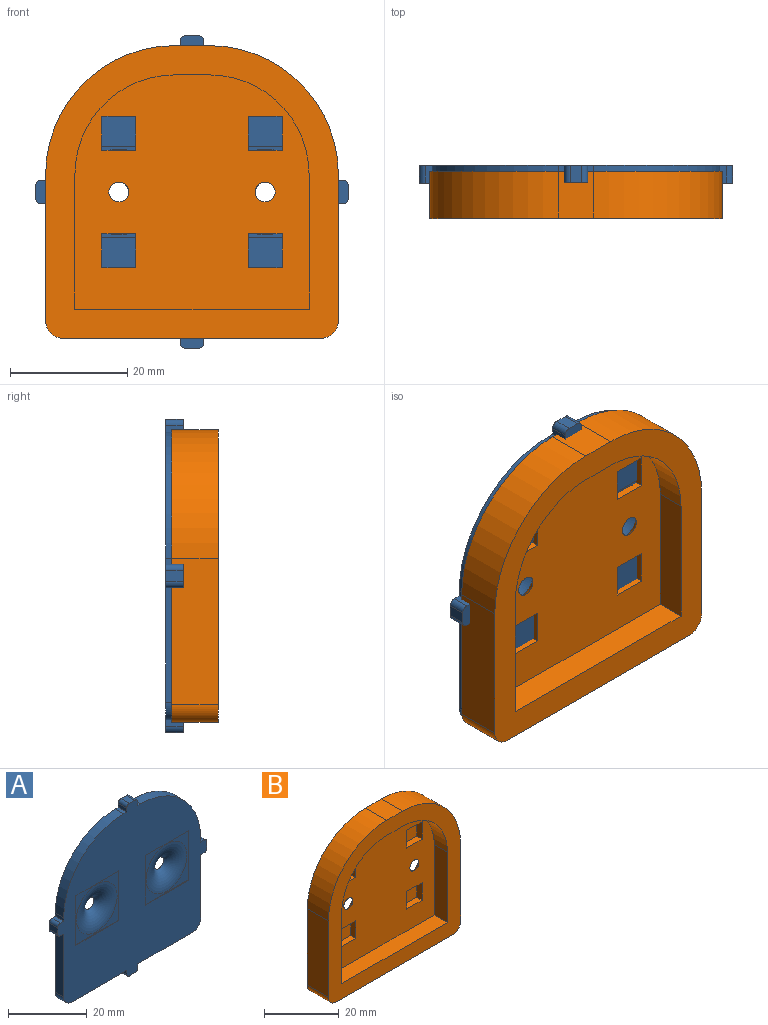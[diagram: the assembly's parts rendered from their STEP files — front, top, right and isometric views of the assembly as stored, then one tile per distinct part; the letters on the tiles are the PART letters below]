
ASSEMBLY  parts=2 mates=1
PART A: 66 faces, bbox 53.5x7.2x53.5 mm
  f0: plane 53.5x53.5mm, normal (0,-1,0), area 1767.7mm2, adj f2,f3,f4,f5,f6,f7,f8,f9
  f1: plane 53.5x53.5mm, normal (0,1,0), area 2089.3mm2, adj f2,f3,f4,f5,f6,f7,f8,f9
  f2: plane 19.55x3mm, normal (0,0,-1), area 58.6mm2, adj f0,f1,f3,f24
  f3: plane 3x1.2mm, normal (-1,0,0), area 3.6mm2, adj f0,f1,f2,f58
  f4: plane 3x2mm, normal (0,0,-1), area 6mm2, adj f0,f1,f58,f59
  f5: plane 3x1.2mm, normal (1,0,0), area 3.6mm2, adj f0,f1,f6,f59
  f6: plane 19.55x3mm, normal (0,0,-1), area 58.6mm2, adj f0,f1,f5,f25
  f7: plane 19.55x3mm, normal (1,0,0), area 58.6mm2, adj f0,f1,f8,f25
  f8: plane 3x1.2mm, normal (0,0,-1), area 3.6mm2, adj f0,f1,f7,f62
  f9: plane 3x2mm, normal (1,0,0), area 6mm2, adj f0,f1,f62,f63
  f10: plane 3x1.2mm, normal (0,0,1), area 3.6mm2, adj f0,f1,f11,f63
  f11: plane 3x1.05mm, normal (1,0,0), area 3.1mm2, adj f0,f1,f10,f12
  f12: cylinder r=21.5mm len=21.5mm, axis (0,1,0), area 101.3mm2, adj f0,f1,f11,f13
  f13: plane 3x1.05mm, normal (0,0,1), area 3.1mm2, adj f0,f1,f12,f14
  f14: plane 3x1.2mm, normal (1,0,0), area 3.6mm2, adj f0,f1,f13,f60
  f15: plane 3x2mm, normal (0,0,1), area 6mm2, adj f0,f1,f60,f61
  f16: plane 3x1.2mm, normal (-1,0,0), area 3.6mm2, adj f0,f1,f17,f61
  f17: plane 3x1.05mm, normal (0,0,1), area 3.2mm2, adj f0,f1,f16,f18
  f18: cylinder r=21.5mm len=21.5mm, axis (0,1,0), area 101.3mm2, adj f0,f1,f17,f19
  f19: plane 3x1.05mm, normal (-1,0,0), area 3.1mm2, adj f0,f1,f18,f20
  f20: plane 3x1.2mm, normal (0,0,1), area 3.6mm2, adj f0,f1,f19,f64
  f21: plane 3x2mm, normal (-1,0,0), area 6mm2, adj f0,f1,f64,f65
  f22: plane 3x1.2mm, normal (0,0,-1), area 3.6mm2, adj f0,f1,f23,f65
  f23: plane 19.55x3mm, normal (-1,0,0), area 58.6mm2, adj f0,f1,f22,f24
  f24: cylinder r=3mm len=3mm, axis (0,1,0), area 14.1mm2, adj f0,f1,f2,f23
  f25: cylinder r=3mm len=3mm, axis (0,-1,0), area 14.1mm2, adj f0,f1,f6,f7
  f26: plane 5.8x2mm, normal (0,0,1), area 11.6mm2, adj f1,f27,f29,f30
  f27: plane 5.8x2mm, normal (1,0,0), area 11.6mm2, adj f1,f26,f28,f30
  f28: plane 5.8x2mm, normal (0,0,-1), area 11.6mm2, adj f1,f27,f29,f30
  f29: plane 5.8x2mm, normal (-1,0,0), area 11.6mm2, adj f1,f26,f28,f30
  f30: plane 5.8x5.8mm, normal (0,1,0), area 33.6mm2, adj f26,f27,f28,f29
  f31: plane 5.8x2mm, normal (1,0,0), area 11.6mm2, adj f1,f32,f34,f35
  f32: plane 5.8x2mm, normal (0,0,-1), area 11.6mm2, adj f1,f31,f33,f35
  f33: plane 5.8x2mm, normal (-1,0,0), area 11.6mm2, adj f1,f32,f34,f35
  f34: plane 5.8x2mm, normal (0,0,1), area 11.6mm2, adj f1,f31,f33,f35
  f35: plane 5.8x5.8mm, normal (0,1,0), area 33.6mm2, adj f31,f32,f33,f34
  f36: plane 5.8x2mm, normal (0,0,1), area 11.6mm2, adj f1,f37,f39,f40
  f37: plane 5.8x2mm, normal (1,0,0), area 11.6mm2, adj f1,f36,f38,f40
  f38: plane 5.8x2mm, normal (0,0,-1), area 11.6mm2, adj f1,f37,f39,f40
  f39: plane 5.8x2mm, normal (-1,0,0), area 11.6mm2, adj f1,f36,f38,f40
  f40: plane 5.8x5.8mm, normal (0,1,0), area 33.6mm2, adj f36,f37,f38,f39
  f41: plane 5.8x2mm, normal (0,0,1), area 11.6mm2, adj f1,f42,f44,f45
  f42: plane 5.8x2mm, normal (1,0,0), area 11.6mm2, adj f1,f41,f43,f45
  f43: plane 5.8x2mm, normal (0,0,-1), area 11.6mm2, adj f1,f42,f44,f45
  f44: plane 5.8x2mm, normal (-1,0,0), area 11.6mm2, adj f1,f41,f43,f45
  f45: plane 5.8x5.8mm, normal (0,1,0), area 33.6mm2, adj f41,f42,f43,f44
  f46: plane 15.4x0.2mm, normal (0,0,-1), area 3.1mm2, adj f0,f47,f49,f50
  f47: plane 15.4x0.2mm, normal (1,0,0), area 3.1mm2, adj f0,f46,f48,f50
  f48: plane 15.4x0.2mm, normal (0,0,1), area 3.1mm2, adj f0,f47,f49,f50
  f49: plane 15.4x0.2mm, normal (-1,0,0), area 3.1mm2, adj f0,f46,f48,f50
  f50: plane 15.4x15.4mm, normal (0,-1,0), area 69.7mm2, adj f46,f47,f48,f49,f56
  f51: plane 15.4x0.2mm, normal (0,0,-1), area 3.1mm2, adj f0,f52,f54,f55
  f52: plane 15.4x0.2mm, normal (1,0,0), area 3.1mm2, adj f0,f51,f53,f55
  f53: plane 15.4x0.2mm, normal (0,0,1), area 3.1mm2, adj f0,f52,f54,f55
  f54: plane 15.4x0.2mm, normal (-1,0,0), area 3.1mm2, adj f0,f51,f53,f55
  f55: plane 15.4x15.4mm, normal (0,-1,0), area 69.7mm2, adj f51,f52,f53,f54,f57
  f56: torus R=7.3mm, axis (0,-1,0), area 174.6mm2, adj f1,f50
  f57: torus R=7.3mm, axis (0,-1,0), area 174.6mm2, adj f1,f55
  f58: cylinder r=1mm len=3mm, axis (0,1,0), area 4.7mm2, adj f0,f1,f3,f4
  f59: cylinder r=1mm len=3mm, axis (0,-1,0), area 4.7mm2, adj f0,f1,f4,f5
  f60: cylinder r=1mm len=3mm, axis (0,1,0), area 4.7mm2, adj f0,f1,f14,f15
  f61: cylinder r=1mm len=3mm, axis (0,-1,0), area 4.7mm2, adj f0,f1,f15,f16
  f62: cylinder r=1mm len=3mm, axis (0,-1,0), area 4.7mm2, adj f0,f1,f8,f9
  f63: cylinder r=1mm len=3mm, axis (0,1,0), area 4.7mm2, adj f0,f1,f9,f10
  f64: cylinder r=1mm len=3mm, axis (0,-1,0), area 4.7mm2, adj f0,f1,f20,f21
  f65: cylinder r=1mm len=3mm, axis (0,1,0), area 4.7mm2, adj f0,f1,f21,f22
PART B: 49 faces, bbox 50x8x50 mm
  f0: plane 40x40mm, normal (0,-1,0), area 1323.2mm2, adj f8,f9,f10,f11,f12,f13,f27,f28
  f1: plane 50x50mm, normal (0,1,0), area 1814.1mm2, adj f2,f3,f4,f5,f6,f7,f15,f16
  f2: plane 8x6mm, normal (0,0,1), area 48mm2, adj f1,f3,f7,f14
  f3: cylinder r=22mm len=22mm, axis (0,1,0), area 276.5mm2, adj f1,f2,f4,f14
  f4: plane 25x8mm, normal (-1,0,0), area 200mm2, adj f1,f3,f14,f26
  f5: plane 44x8mm, normal (0,0,-1), area 352mm2, adj f1,f14,f25,f26
  f6: plane 25x8mm, normal (1,0,0), area 200mm2, adj f1,f7,f14,f25
  f7: cylinder r=22mm len=22mm, axis (0,1,0), area 276.5mm2, adj f1,f2,f6,f14
  f8: plane 40x5mm, normal (0,0,1), area 200mm2, adj f0,f9,f13,f14
  f9: plane 23x5mm, normal (1,0,0), area 115mm2, adj f0,f8,f10,f14
  f10: cylinder r=17mm len=17mm, axis (0,1,0), area 133.5mm2, adj f0,f9,f11,f14
  f11: plane 6x5mm, normal (0,0,-1), area 30mm2, adj f0,f10,f12,f14
  f12: cylinder r=17mm len=17mm, axis (0,1,0), area 133.5mm2, adj f0,f11,f13,f14
  f13: plane 23x5mm, normal (-1,0,0), area 115mm2, adj f0,f8,f12,f14
  f14: plane 50x50mm, normal (0,-1,0), area 812.4mm2, adj f2,f3,f4,f5,f6,f7,f8,f9
  f15: plane 15.4x0.2mm, normal (0,0,-1), area 3.1mm2, adj f1,f16,f18,f19
  f16: plane 15.4x0.2mm, normal (-1,0,0), area 3.1mm2, adj f1,f15,f17,f19
  f17: plane 15.4x0.2mm, normal (0,0,1), area 3.1mm2, adj f1,f16,f18,f19
  f18: plane 15.4x0.2mm, normal (1,0,0), area 3.1mm2, adj f1,f15,f17,f19
  f19: plane 15.4x15.4mm, normal (0,1,0), area 69.7mm2, adj f15,f16,f17,f18,f47
  f20: plane 15.4x0.2mm, normal (0,0,-1), area 3.1mm2, adj f1,f21,f23,f24
  f21: plane 15.4x0.2mm, normal (-1,0,0), area 3.1mm2, adj f1,f20,f22,f24
  f22: plane 15.4x0.2mm, normal (0,0,1), area 3.1mm2, adj f1,f21,f23,f24
  f23: plane 15.4x0.2mm, normal (1,0,0), area 3.1mm2, adj f1,f20,f22,f24
  f24: plane 15.4x15.4mm, normal (0,1,0), area 69.7mm2, adj f20,f21,f22,f23,f48
  f25: cylinder r=3mm len=8mm, axis (0,-1,0), area 37.7mm2, adj f1,f5,f6,f14
  f26: cylinder r=3mm len=8mm, axis (0,1,0), area 37.7mm2, adj f1,f4,f5,f14
  f27: plane 5.8x2mm, normal (0,0,1), area 11.6mm2, adj f0,f28,f30,f31
  f28: plane 5.8x2mm, normal (-1,0,0), area 11.6mm2, adj f0,f27,f29,f31
  f29: plane 5.8x2mm, normal (0,0,-1), area 11.6mm2, adj f0,f28,f30,f31
  f30: plane 5.8x2mm, normal (1,0,0), area 11.6mm2, adj f0,f27,f29,f31
  f31: plane 5.8x5.8mm, normal (0,-1,0), area 33.6mm2, adj f27,f28,f29,f30
  f32: plane 5.8x2mm, normal (0,0,1), area 11.6mm2, adj f0,f33,f35,f36
  f33: plane 5.8x2mm, normal (-1,0,0), area 11.6mm2, adj f0,f32,f34,f36
  f34: plane 5.8x2mm, normal (0,0,-1), area 11.6mm2, adj f0,f33,f35,f36
  f35: plane 5.8x2mm, normal (1,0,0), area 11.6mm2, adj f0,f32,f34,f36
  f36: plane 5.8x5.8mm, normal (0,-1,0), area 33.6mm2, adj f32,f33,f34,f35
  f37: plane 5.8x2mm, normal (0,0,1), area 11.6mm2, adj f0,f38,f40,f41
  f38: plane 5.8x2mm, normal (-1,0,0), area 11.6mm2, adj f0,f37,f39,f41
  f39: plane 5.8x2mm, normal (0,0,-1), area 11.6mm2, adj f0,f38,f40,f41
  f40: plane 5.8x2mm, normal (1,0,0), area 11.6mm2, adj f0,f37,f39,f41
  f41: plane 5.8x5.8mm, normal (0,-1,0), area 33.6mm2, adj f37,f38,f39,f40
  f42: plane 5.8x2mm, normal (0,0,1), area 11.6mm2, adj f0,f43,f45,f46
  f43: plane 5.8x2mm, normal (-1,0,0), area 11.6mm2, adj f0,f42,f44,f46
  f44: plane 5.8x2mm, normal (0,0,-1), area 11.6mm2, adj f0,f43,f45,f46
  f45: plane 5.8x2mm, normal (1,0,0), area 11.6mm2, adj f0,f42,f44,f46
  f46: plane 5.8x5.8mm, normal (0,-1,0), area 33.6mm2, adj f42,f43,f44,f45
  f47: torus R=7.3mm, axis (0,1,0), area 174.6mm2, adj f0,f19
  f48: torus R=7.3mm, axis (0,1,0), area 174.6mm2, adj f0,f24
PLACE A t=(30.06,37.25,-49.77)mm
PLACE B t=(76.09,36.25,-29.18)mm
MATE fastened A.f35 <-> B.f36  axis (0,1,0) through (93.3,35.25,-24.14)mm
